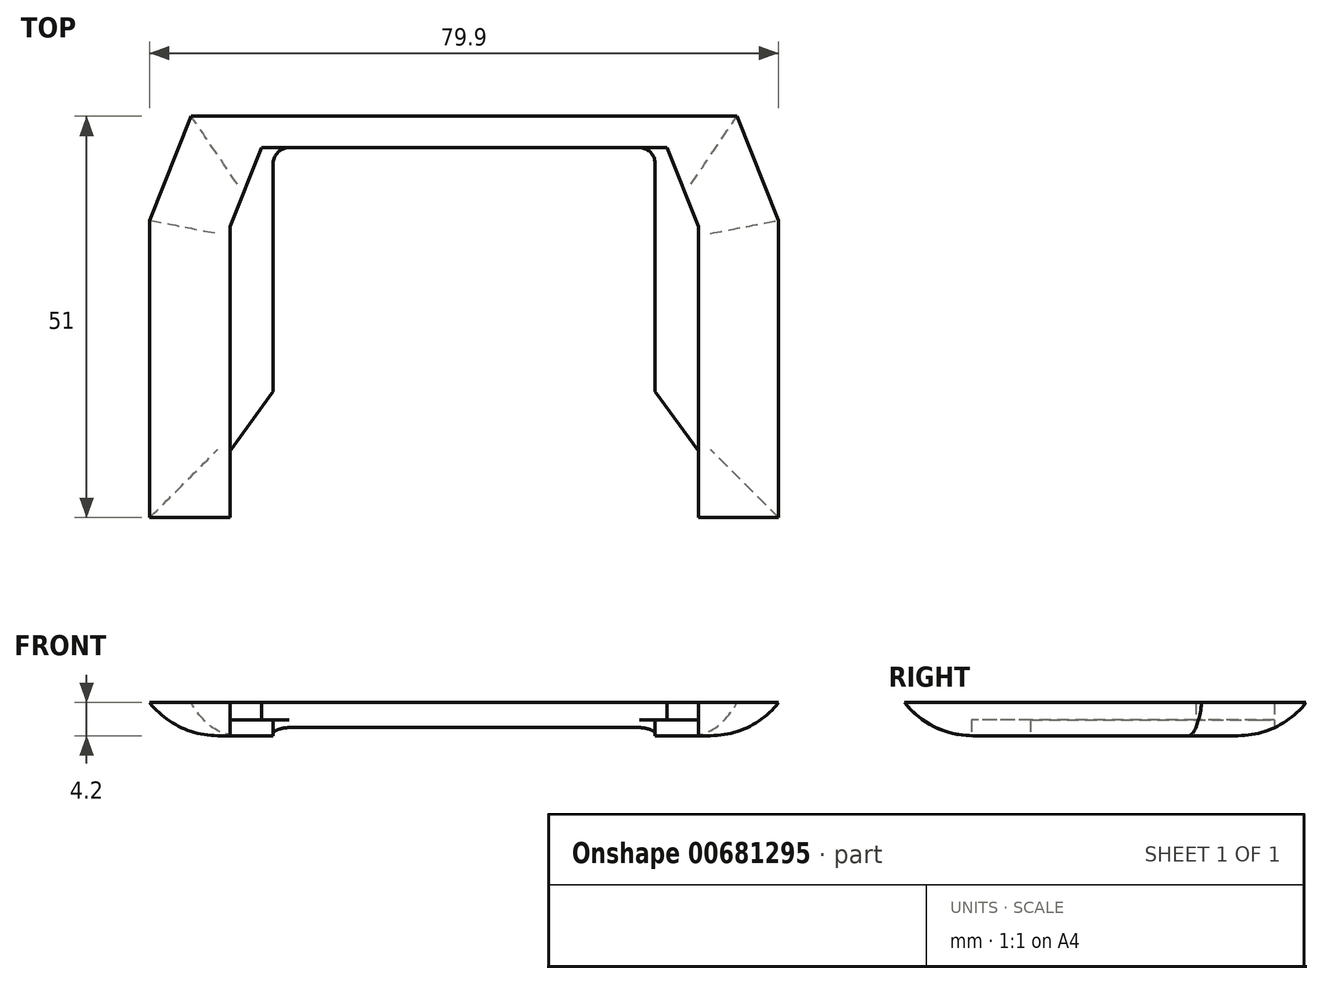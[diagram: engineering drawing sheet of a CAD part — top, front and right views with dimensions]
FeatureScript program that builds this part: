
annotation { "Feature Type Name" : "Feature", "Feature Type Description" : "" }
export const myFeature = defineFeature(function(context is Context, id is Id, definition is map)
    precondition{}
    {
        {
            var Q0;
            Q0=qCreatedBy(makeId("Top.planeOp"),FACE);
            var sketch = newSketch(context, id + "F0", { "sketchPlane" : qUnion([Q0])});
            skLineSegment(sketch, "E0.bottom", {"start": v(-25.5, 14.25) * mm, "end": v(26, 14.25) * mm});
            skLineSegment(sketch, "E0.left", {"start": v(-29.5, 4.25) * mm, "end": v(-29.5, -35.75) * mm});
            skLineSegment(sketch, "E0.right", {"start": v(30, 4.25) * mm, "end": v(30, -35.75) * mm});
            skLineSegment(sketch, "E1", {"start": v(-25.5, 14.25) * mm, "end": v(-29.5, 4.25) * mm});
            skPoint(sketch, "E2.orphan", {"position": v(-29.5, 14.25) * mm});
            skLineSegment(sketch, "E3", {"start": v(26, 14.25) * mm, "end": v(30, 4.25) * mm});
            skPoint(sketch, "E4.orphan", {"position": v(30, 14.25) * mm});
            skLineSegment(sketch, "E5.0", {"start": v(-28.2, 18.25) * mm, "end": v(-33.5, 5.02) * mm});
            skLineSegment(sketch, "E5.1", {"start": v(-33.5, -32.75) * mm, "end": v(34, -32.75) * mm});
            skLineSegment(sketch, "E5.2", {"start": v(34, 5.02) * mm, "end": v(34, -32.75) * mm});
            skLineSegment(sketch, "E5.3", {"start": v(-33.5, 5.02) * mm, "end": v(-33.5, -32.75) * mm});
            skLineSegment(sketch, "E5.4", {"start": v(28.7, 18.25) * mm, "end": v(34, 5.02) * mm});
            skLineSegment(sketch, "E5.5", {"start": v(-28.2, 18.25) * mm, "end": v(28.7, 18.25) * mm});
            skLineSegment(sketch, "E6", {"start": v(-29.5, -32.75) * mm, "end": v(-29.5, -35.75) * mm});
            skLineSegment(sketch, "E7", {"start": v(30, -32.75) * mm, "end": v(30, -35.75) * mm});
            skLineSegment(sketch, "E8.bottom", {"start": v(-29.5, -32.75) * mm, "end": v(30, -32.75) * mm});
            skLineSegment(sketch, "E8.left", {"start": v(-29.5, -32.75) * mm, "end": v(-29.5, -24.25) * mm});
            skLineSegment(sketch, "E8.right", {"start": v(30, -32.75) * mm, "end": v(30, -24.25) * mm});
            skLineSegment(sketch, "E9.top", {"start": v(-22, 14.25) * mm, "end": v(22.5, 14.25) * mm});
            skLineSegment(sketch, "E9.left", {"start": v(-24, -16.75) * mm, "end": v(-24, 12.25) * mm});
            skLineSegment(sketch, "E9.right", {"start": v(24.5, -16.75) * mm, "end": v(24.5, 12.25) * mm});
            skPoint(sketch, "E10.visualSharp", {"position": v(-24, 14.25) * mm});
            skArc(sketch, "E10.filletArc", {"start": v(-22, 14.25) * mm, "mid": v(-23.41, 13.66) * mm, "end": v(-24, 12.25) * mm});
            skPoint(sketch, "E11.visualSharp", {"position": v(24.5, 14.25) * mm});
            skArc(sketch, "E11.filletArc", {"start": v(24.5, 12.25) * mm, "mid": v(23.91, 13.66) * mm, "end": v(22.5, 14.25) * mm});
            skLineSegment(sketch, "E12", {"start": v(24.5, -16.75) * mm, "end": v(30, -24.25) * mm});
            skLineSegment(sketch, "E13", {"start": v(-24, -16.75) * mm, "end": v(-29.5, -24.25) * mm});
            skPoint(sketch, "E14.orphan", {"position": v(-29.5, -15.75) * mm});
            skPoint(sketch, "E15.orphan", {"position": v(30, -15.75) * mm});
            skSolve(sketch);
        }
        {
            var Q0;
            Q0=makeQuery(id+"F0.imprint","IMPRINT",FACE,{"disambiguationData":[TD([[makeQuery(id+"F0.imprint","IMPRINT",EDGE,{"derivedFrom":sQuery(id+"F0.wireOp",EDGE,"E0.bottom")}),-1.0]])]});
            extrude(context, id + "F1", {"entities" : qUnion([Q0]), "depth" : 2 * mm, "offsetDistance" : 25 * mm});
        }
        {
            var Q0;
            Q0=makeQuery(id+"F0.imprint","IMPRINT",FACE,{"disambiguationData":[TD([[makeQuery(id+"F0.imprint","IMPRINT",EDGE,{"derivedFrom":sQuery(id+"F0.wireOp",EDGE,"E0.bottom")}),1.0]])]});
            extrude(context, id + "F2", {"entities" : qUnion([Q0]), "operationType" : NewBodyOperationType.ADD, "depth" : 4.2 * mm, "offsetDistance" : 25 * mm});
        }
        {
            var Q0;
            {var subQ0=sQuery(id+"F0.wireOp",EDGE,"E5.1");Q0=makeQuery(id+"F2.opExtrude","CAP_EDGE",EDGE,{"disambiguationData":[OSD([subQ0]),TDD([makeQuery(id+"F0.imprint","IMPRINT",EDGE,{"disambiguationData":[TD([[makeQuery(id+"F0.imprint","INTERSECT",VERTEX,{"derivedFrom":[subQ0,sQuery(id+"F0.wireOp",EDGE,"E5.2")]}),1.0]])],"derivedFrom":subQ0})])],"isStart":true});}
            var Q1;
            Q1=makeQuery(id+"F2.opExtrude","CAP_EDGE",EDGE,{"disambiguationData":[OSD([sQuery(id+"F0.wireOp",EDGE,"E5.5")])],"isStart":true});
            var Q2;
            {var subQ0=sQuery(id+"F0.wireOp",EDGE,"E5.1");Q2=makeQuery(id+"F2.opExtrude","CAP_EDGE",EDGE,{"disambiguationData":[OSD([subQ0]),TDD([makeQuery(id+"F0.imprint","IMPRINT",EDGE,{"disambiguationData":[TD([[makeQuery(id+"F0.imprint","INTERSECT",VERTEX,{"derivedFrom":[subQ0,sQuery(id+"F0.wireOp",EDGE,"E5.3")]}),-1.0]])],"derivedFrom":subQ0})])],"isStart":true});}
            fillet(context, id + "F3", {"entities" : qUnion([Q0, Q1, Q2]), "radius" : 11 * mm, "tangentPropagation" : true, "allowEdgeOverflow" : false});
        }
        {
            var Q0;
            Q0=makeQuery(id+"F2.opExtrude","SWEPT_FACE",FACE,{"disambiguationData":[OSD([sQuery(id+"F0.wireOp",EDGE,"E5.3")])]});
            var Q1;
            Q1=makeQuery(id+"F2.opExtrude","SWEPT_FACE",FACE,{"disambiguationData":[OSD([sQuery(id+"F0.wireOp",EDGE,"E5.0")])]});
            extrude(context, id + "F4", {"entities" : qUnion([Q0, Q1]), "operationType" : NewBodyOperationType.ADD, "depth" : 6.2 * mm, "offsetDistance" : 25 * mm});
        }
        {
            var Q0;
            {var subQ0=sQuery(id+"F0.wireOp",EDGE,"E5.3");Q0=makeQuery(id+"F4.opExtrude","CAP_EDGE",EDGE,{"disambiguationData":[OSD([subQ0]),TDD([makeQuery(id+"F2.opExtrude","CAP_EDGE",EDGE,{"disambiguationData":[OSD([subQ0])],"isStart":true})])],"isStart":false});}
            var Q1;
            Q1=makeQuery(id+"F4.opExtrude","CAP_EDGE",EDGE,{"disambiguationData":[OSD([sQuery(id+"F0.wireOp",EDGE,"E5.0"),sQuery(id+"F0.wireOp",EDGE,"E5.5")]),OD(0.0)],"isStart":false});
            fillet(context, id + "F5", {"entities" : qUnion([Q0, Q1]), "radius" : 11 * mm, "tangentPropagation" : true, "allowEdgeOverflow" : false});
        }
        {
            var Q0;
            Q0=makeQuery(id+"F2.opExtrude","SWEPT_FACE",FACE,{"disambiguationData":[OSD([sQuery(id+"F0.wireOp",EDGE,"E5.2")])]});
            var Q1;
            Q1=makeQuery(id+"F2.opExtrude","SWEPT_FACE",FACE,{"disambiguationData":[OSD([sQuery(id+"F0.wireOp",EDGE,"E5.4")])]});
            extrude(context, id + "F6", {"entities" : qUnion([Q0, Q1]), "operationType" : NewBodyOperationType.ADD, "depth" : 6.2 * mm, "offsetDistance" : 25 * mm});
        }
        {
            var Q0;
            {var subQ0=sQuery(id+"F0.wireOp",EDGE,"E5.4");Q0=makeQuery(id+"F6.opExtrude","CAP_EDGE",EDGE,{"disambiguationData":[OSD([subQ0]),TDD([makeQuery(id+"F2.opExtrude","CAP_EDGE",EDGE,{"disambiguationData":[OSD([subQ0])],"isStart":true})]),OD(1.0)],"isStart":false});}
            var Q1;
            {var subQ0=sQuery(id+"F0.wireOp",EDGE,"E5.2");Q1=makeQuery(id+"F6.opExtrude","CAP_EDGE",EDGE,{"disambiguationData":[OSD([subQ0]),TDD([makeQuery(id+"F2.opExtrude","CAP_EDGE",EDGE,{"disambiguationData":[OSD([subQ0])],"isStart":true})])],"isStart":false});}
            fillet(context, id + "F7", {"entities" : qUnion([Q0, Q1]), "radius" : 11 * mm, "tangentPropagation" : true, "allowEdgeOverflow" : false});
        }
    });
